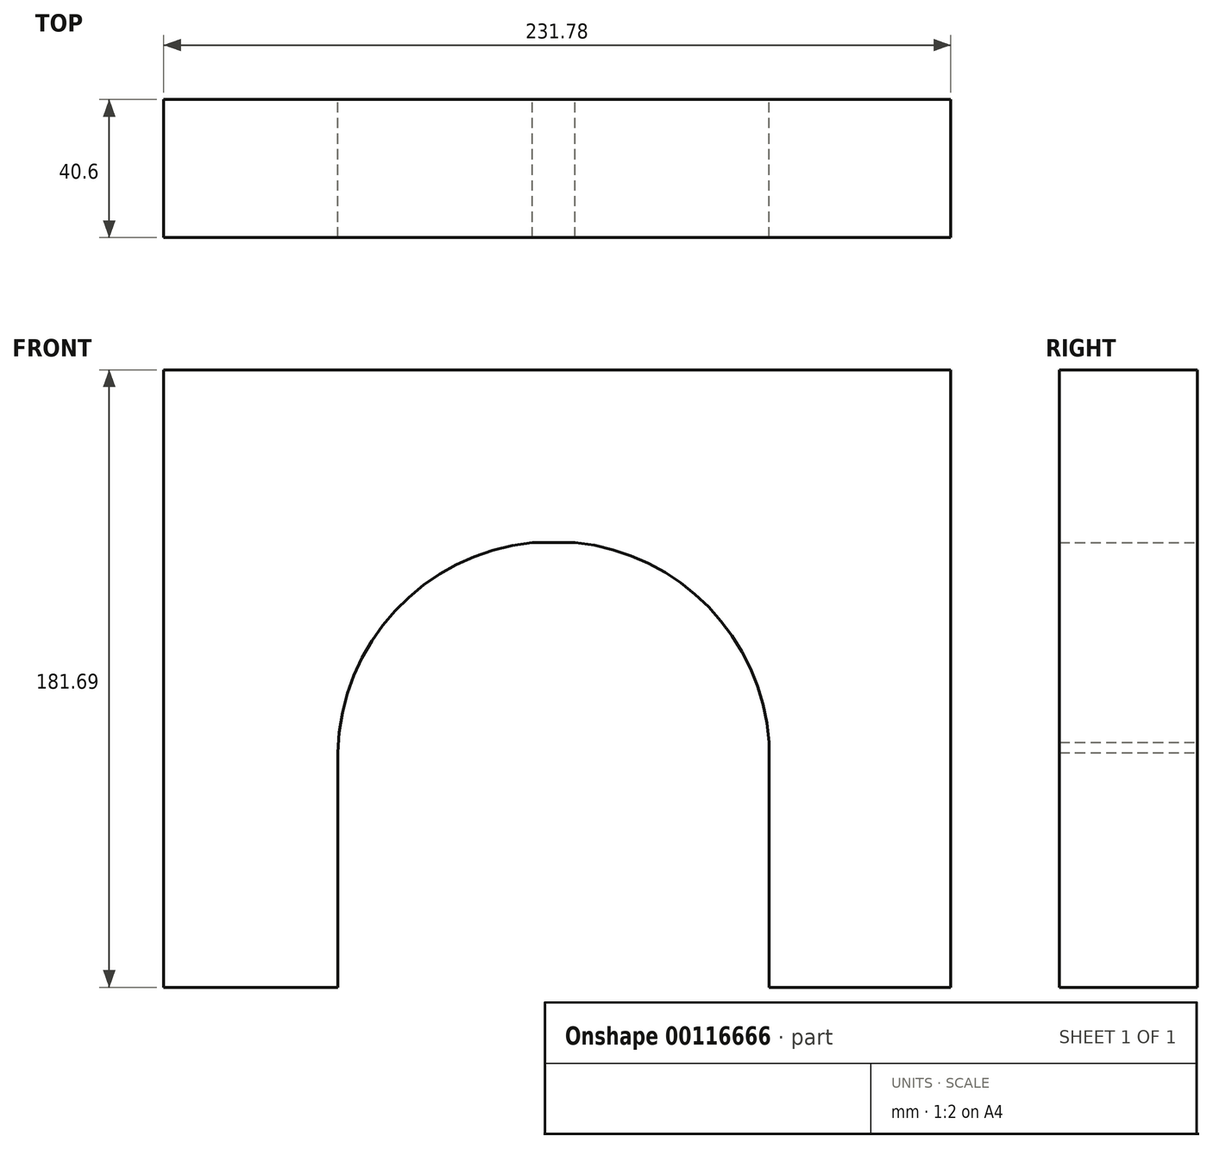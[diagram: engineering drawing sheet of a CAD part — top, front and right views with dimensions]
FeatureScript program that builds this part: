
annotation { "Feature Type Name" : "Feature", "Feature Type Description" : "" }
export const myFeature = defineFeature(function(context is Context, id is Id, definition is map)
    precondition{}
    {
        {
            var Q0;
            Q0=qCreatedBy(makeId("Front.planeOp"),FACE);
            var sketch = newSketch(context, id + "F0", { "sketchPlane" : qUnion([Q0])});
            skLineSegment(sketch, "E0.bottom", {"start": v(-63.65, 61.24) * mm, "end": v(63.35, 61.24) * mm});
            skLineSegment(sketch, "E0.top", {"start": v(-63.65, 10.44) * mm, "end": v(63.35, 10.44) * mm});
            skLineSegment(sketch, "E0.left", {"start": v(-63.65, 61.24) * mm, "end": v(-63.65, 10.44) * mm});
            skLineSegment(sketch, "E0.right", {"start": v(63.35, 61.24) * mm, "end": v(63.35, 10.44) * mm});
            skArc(sketch, "E1", {"start": v(63.35, -48.42) * mm, "mid": v(-1.57, 10.74) * mm, "end": v(-63.65, -51.4) * mm});
            skLineSegment(sketch, "E2", {"start": v(-63.65, 10.44) * mm, "end": v(-63.65, -51.4) * mm});
            skLineSegment(sketch, "E3", {"start": v(63.35, 10.44) * mm, "end": v(63.35, -48.42) * mm});
            skLineSegment(sketch, "E4.bottom", {"start": v(-63.65, 61.24) * mm, "end": v(-90.81, 61.24) * mm});
            skLineSegment(sketch, "E4.top", {"start": v(-63.65, -51.89) * mm, "end": v(-90.81, -51.89) * mm});
            skLineSegment(sketch, "E4.left", {"start": v(-63.65, 61.24) * mm, "end": v(-63.65, -51.89) * mm});
            skLineSegment(sketch, "E4.right", {"start": v(-90.81, 61.24) * mm, "end": v(-90.81, -51.89) * mm});
            skLineSegment(sketch, "E5.bottom", {"start": v(63.35, 61.24) * mm, "end": v(85.97, 61.24) * mm});
            skLineSegment(sketch, "E5.top", {"start": v(63.35, -51.89) * mm, "end": v(85.97, -51.89) * mm});
            skLineSegment(sketch, "E5.left", {"start": v(63.35, 61.24) * mm, "end": v(63.35, -51.89) * mm});
            skLineSegment(sketch, "E5.right", {"start": v(85.97, 61.24) * mm, "end": v(85.97, -51.89) * mm});
            skSolve(sketch);
        }
        {
            var Q0;
            Q0 = qSketchRegion(id + "F0", true);
            extrude(context, id + "F1", {"entities" : qUnion([Q0]), "depth" : 40.6 * mm});
        }
        {
            var Q0;
            Q0=makeQuery(id+"F1.opExtrude","SWEPT_FACE",FACE,{"disambiguationData":[OSD([sQuery(id+"F0.wireOp",EDGE,"E4.top")])]});
            var Q1;
            Q1=makeQuery(id+"F1.opExtrude","SWEPT_FACE",FACE,{"disambiguationData":[OSD([sQuery(id+"F0.wireOp",EDGE,"E5.top")])]});
            extrude(context, id + "F2", {"entities" : qUnion([Q0, Q1]), "operationType" : NewBodyOperationType.ADD, "depth" : 68.57 * mm});
        }
        {
            var Q0;
            {var subQ0=sQuery(id+"F0.wireOp",EDGE,"E5.right");Q0=makeQuery(id+"F2.boolean.opBoolean","MERGE",FACE,{"derivedFrom":[makeQuery(id+"F1.opExtrude","SWEPT_FACE",FACE,{"disambiguationData":[OSD([subQ0])]}),makeQuery(id+"F2.opExtrude","SWEPT_FACE",FACE,{"disambiguationData":[OSD([sQuery(id+"F0.wireOp",EDGE,"E5.top"),subQ0])]})]});}
            extrude(context, id + "F3", {"entities" : qUnion([Q0]), "operationType" : NewBodyOperationType.ADD, "depth" : 30.88 * mm});
        }
        {
            var Q0;
            {var subQ0=sQuery(id+"F0.wireOp",EDGE,"E4.right");Q0=makeQuery(id+"F2.boolean.opBoolean","MERGE",FACE,{"derivedFrom":[makeQuery(id+"F1.opExtrude","SWEPT_FACE",FACE,{"disambiguationData":[OSD([subQ0])]}),makeQuery(id+"F2.opExtrude","SWEPT_FACE",FACE,{"disambiguationData":[OSD([sQuery(id+"F0.wireOp",EDGE,"E4.top"),subQ0])]})]});}
            extrude(context, id + "F4", {"entities" : qUnion([Q0]), "operationType" : NewBodyOperationType.ADD, "depth" : 24.1 * mm});
        }
    });
